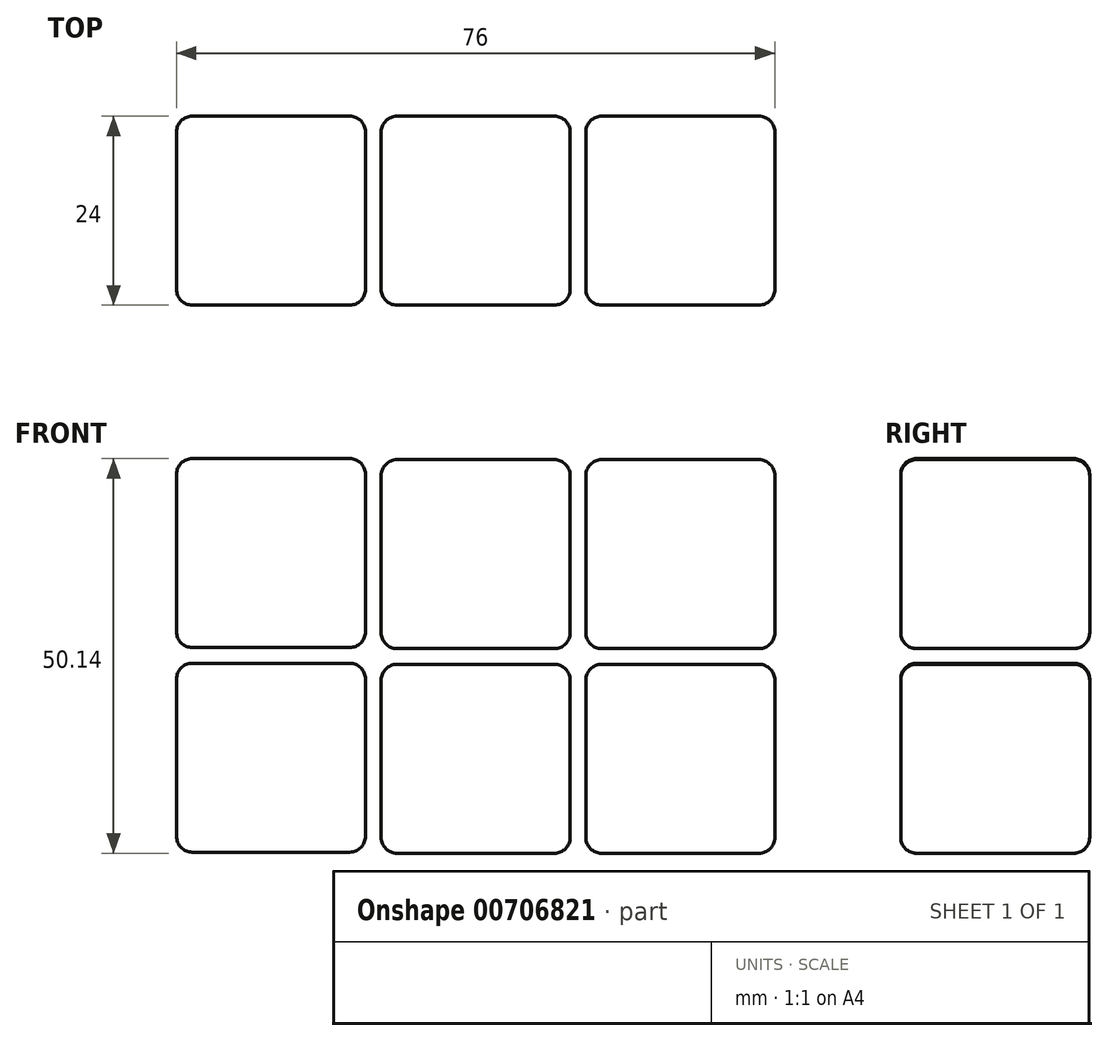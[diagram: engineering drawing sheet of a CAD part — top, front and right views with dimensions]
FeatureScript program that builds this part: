
annotation { "Feature Type Name" : "Feature", "Feature Type Description" : "" }
export const myFeature = defineFeature(function(context is Context, id is Id, definition is map)
    precondition{}
    {
        {
            var Q0;
            Q0=qCreatedBy(makeId("Front.planeOp"),FACE);
            var sketch = newSketch(context, id + "F0", { "sketchPlane" : qUnion([Q0])});
            skLineSegment(sketch, "E0.bottom", {"start": v(-63.14, 48.94) * mm, "end": v(-43.14, 48.94) * mm});
            skLineSegment(sketch, "E0.top", {"start": v(-63.14, 24.94) * mm, "end": v(-43.14, 24.94) * mm});
            skLineSegment(sketch, "E0.left", {"start": v(-65.14, 46.94) * mm, "end": v(-65.14, 26.94) * mm});
            skLineSegment(sketch, "E0.right", {"start": v(-41.14, 46.94) * mm, "end": v(-41.14, 26.94) * mm});
            skPoint(sketch, "E1.visualSharp", {"position": v(-65.14, 48.94) * mm});
            skArc(sketch, "E1.filletArc", {"start": v(-63.14, 48.94) * mm, "mid": v(-64.55, 48.36) * mm, "end": v(-65.14, 46.94) * mm});
            skPoint(sketch, "E2.visualSharp", {"position": v(-41.14, 48.94) * mm});
            skArc(sketch, "E2.filletArc", {"start": v(-41.14, 46.94) * mm, "mid": v(-41.72, 48.36) * mm, "end": v(-43.14, 48.94) * mm});
            skPoint(sketch, "E3.visualSharp", {"position": v(-41.14, 24.94) * mm});
            skArc(sketch, "E3.filletArc", {"start": v(-43.14, 24.94) * mm, "mid": v(-41.72, 25.53) * mm, "end": v(-41.14, 26.94) * mm});
            skPoint(sketch, "E4.visualSharp", {"position": v(-65.14, 24.94) * mm});
            skArc(sketch, "E4.filletArc", {"start": v(-65.14, 26.94) * mm, "mid": v(-64.55, 25.53) * mm, "end": v(-63.14, 24.94) * mm});
            skLineSegment(sketch, "E5.bottom", {"start": v(-63.14, 22.94) * mm, "end": v(-43.14, 22.94) * mm});
            skLineSegment(sketch, "E5.top", {"start": v(-63.14, -1.06) * mm, "end": v(-43.14, -1.06) * mm});
            skLineSegment(sketch, "E5.left", {"start": v(-65.14, 20.94) * mm, "end": v(-65.14, 0.94) * mm});
            skLineSegment(sketch, "E5.right", {"start": v(-41.14, 20.94) * mm, "end": v(-41.14, 0.94) * mm});
            skPoint(sketch, "E6.visualSharp", {"position": v(-65.14, 22.94) * mm});
            skArc(sketch, "E6.filletArc", {"start": v(-63.14, 22.94) * mm, "mid": v(-64.55, 22.36) * mm, "end": v(-65.14, 20.94) * mm});
            skPoint(sketch, "E7.visualSharp", {"position": v(-41.14, 22.94) * mm});
            skArc(sketch, "E7.filletArc", {"start": v(-41.14, 20.94) * mm, "mid": v(-41.72, 22.36) * mm, "end": v(-43.14, 22.94) * mm});
            skPoint(sketch, "E8.visualSharp", {"position": v(-41.14, -1.06) * mm});
            skArc(sketch, "E8.filletArc", {"start": v(-43.14, -1.06) * mm, "mid": v(-41.72, -0.47) * mm, "end": v(-41.14, 0.94) * mm});
            skPoint(sketch, "E9.visualSharp", {"position": v(-65.14, -1.06) * mm});
            skArc(sketch, "E9.filletArc", {"start": v(-65.14, 0.94) * mm, "mid": v(-64.55, -0.47) * mm, "end": v(-63.14, -1.06) * mm});
            skLineSegment(sketch, "E10.bottom", {"start": v(-89.14, 48.94) * mm, "end": v(-69.14, 48.94) * mm});
            skLineSegment(sketch, "E10.top", {"start": v(-89.14, 24.94) * mm, "end": v(-69.14, 24.94) * mm});
            skLineSegment(sketch, "E10.left", {"start": v(-91.14, 46.94) * mm, "end": v(-91.14, 26.94) * mm});
            skLineSegment(sketch, "E10.right", {"start": v(-67.14, 46.94) * mm, "end": v(-67.14, 26.94) * mm});
            skPoint(sketch, "E11.visualSharp", {"position": v(-91.14, 48.94) * mm});
            skArc(sketch, "E11.filletArc", {"start": v(-89.14, 48.94) * mm, "mid": v(-90.55, 48.36) * mm, "end": v(-91.14, 46.94) * mm});
            skPoint(sketch, "E12.visualSharp", {"position": v(-67.14, 48.94) * mm});
            skArc(sketch, "E12.filletArc", {"start": v(-67.14, 46.94) * mm, "mid": v(-67.72, 48.36) * mm, "end": v(-69.14, 48.94) * mm});
            skPoint(sketch, "E13.visualSharp", {"position": v(-67.14, 24.94) * mm});
            skArc(sketch, "E13.filletArc", {"start": v(-69.14, 24.94) * mm, "mid": v(-67.72, 25.53) * mm, "end": v(-67.14, 26.94) * mm});
            skPoint(sketch, "E14.visualSharp", {"position": v(-91.14, 24.94) * mm});
            skArc(sketch, "E14.filletArc", {"start": v(-91.14, 26.94) * mm, "mid": v(-90.55, 25.53) * mm, "end": v(-89.14, 24.94) * mm});
            skLineSegment(sketch, "E15.bottom", {"start": v(-89.14, 22.94) * mm, "end": v(-69.14, 22.94) * mm});
            skLineSegment(sketch, "E15.top", {"start": v(-89.14, -1.06) * mm, "end": v(-69.14, -1.06) * mm});
            skLineSegment(sketch, "E15.left", {"start": v(-91.14, 20.94) * mm, "end": v(-91.14, 0.94) * mm});
            skLineSegment(sketch, "E15.right", {"start": v(-67.14, 20.94) * mm, "end": v(-67.14, 0.94) * mm});
            skPoint(sketch, "E16.visualSharp", {"position": v(-91.14, 22.94) * mm});
            skArc(sketch, "E16.filletArc", {"start": v(-89.14, 22.94) * mm, "mid": v(-90.55, 22.36) * mm, "end": v(-91.14, 20.94) * mm});
            skPoint(sketch, "E17.visualSharp", {"position": v(-67.14, 22.94) * mm});
            skArc(sketch, "E17.filletArc", {"start": v(-67.14, 20.94) * mm, "mid": v(-67.72, 22.36) * mm, "end": v(-69.14, 22.94) * mm});
            skPoint(sketch, "E18.visualSharp", {"position": v(-67.14, -1.06) * mm});
            skArc(sketch, "E18.filletArc", {"start": v(-69.14, -1.06) * mm, "mid": v(-67.72, -0.47) * mm, "end": v(-67.14, 0.94) * mm});
            skPoint(sketch, "E19.visualSharp", {"position": v(-91.14, -1.06) * mm});
            skArc(sketch, "E19.filletArc", {"start": v(-91.14, 0.94) * mm, "mid": v(-90.55, -0.47) * mm, "end": v(-89.14, -1.06) * mm});
            skLineSegment(sketch, "E20.bottom", {"start": v(-115.14, 49.08) * mm, "end": v(-95.14, 49.08) * mm});
            skLineSegment(sketch, "E20.top", {"start": v(-115.14, 25.08) * mm, "end": v(-95.14, 25.08) * mm});
            skLineSegment(sketch, "E20.left", {"start": v(-117.14, 47.08) * mm, "end": v(-117.14, 27.08) * mm});
            skLineSegment(sketch, "E20.right", {"start": v(-93.14, 47.08) * mm, "end": v(-93.14, 27.08) * mm});
            skPoint(sketch, "E21.visualSharp", {"position": v(-117.14, 49.08) * mm});
            skArc(sketch, "E21.filletArc", {"start": v(-115.14, 49.08) * mm, "mid": v(-116.55, 48.5) * mm, "end": v(-117.14, 47.08) * mm});
            skPoint(sketch, "E22.visualSharp", {"position": v(-93.14, 49.08) * mm});
            skArc(sketch, "E22.filletArc", {"start": v(-93.14, 47.08) * mm, "mid": v(-93.72, 48.5) * mm, "end": v(-95.14, 49.08) * mm});
            skPoint(sketch, "E23.visualSharp", {"position": v(-93.14, 25.08) * mm});
            skArc(sketch, "E23.filletArc", {"start": v(-95.14, 25.08) * mm, "mid": v(-93.72, 25.67) * mm, "end": v(-93.14, 27.08) * mm});
            skPoint(sketch, "E24.visualSharp", {"position": v(-117.14, 25.08) * mm});
            skArc(sketch, "E24.filletArc", {"start": v(-117.14, 27.08) * mm, "mid": v(-116.55, 25.67) * mm, "end": v(-115.14, 25.08) * mm});
            skLineSegment(sketch, "E25.bottom", {"start": v(-115.14, 23.08) * mm, "end": v(-95.14, 23.08) * mm});
            skLineSegment(sketch, "E25.top", {"start": v(-115.14, -0.92) * mm, "end": v(-95.14, -0.92) * mm});
            skLineSegment(sketch, "E25.left", {"start": v(-117.14, 21.08) * mm, "end": v(-117.14, 1.08) * mm});
            skLineSegment(sketch, "E25.right", {"start": v(-93.14, 21.08) * mm, "end": v(-93.14, 1.08) * mm});
            skPoint(sketch, "E26.visualSharp", {"position": v(-117.14, 23.08) * mm});
            skArc(sketch, "E26.filletArc", {"start": v(-115.14, 23.08) * mm, "mid": v(-116.55, 22.5) * mm, "end": v(-117.14, 21.08) * mm});
            skPoint(sketch, "E27.visualSharp", {"position": v(-93.14, 23.08) * mm});
            skArc(sketch, "E27.filletArc", {"start": v(-93.14, 21.08) * mm, "mid": v(-93.72, 22.5) * mm, "end": v(-95.14, 23.08) * mm});
            skPoint(sketch, "E28.visualSharp", {"position": v(-93.14, -0.92) * mm});
            skArc(sketch, "E28.filletArc", {"start": v(-95.14, -0.92) * mm, "mid": v(-93.72, -0.33) * mm, "end": v(-93.14, 1.08) * mm});
            skPoint(sketch, "E29.visualSharp", {"position": v(-117.14, -0.92) * mm});
            skArc(sketch, "E29.filletArc", {"start": v(-117.14, 1.08) * mm, "mid": v(-116.55, -0.33) * mm, "end": v(-115.14, -0.92) * mm});
            skSolve(sketch);
        }
        {
            var Q0;
            Q0 = qSketchRegion(id + "F0", true);
            extrude(context, id + "F1", {"entities" : qUnion([Q0]), "depth" : 24 * mm, "offsetDistance" : 25 * mm});
        }
        {
            var Q0;
            Q0=makeQuery(id+"F1.opExtrude","CAP_FACE",FACE,{"disambiguationData":[OSD([sQuery(id+"F0.wireOp",EDGE,"E25.bottom"),sQuery(id+"F0.wireOp",EDGE,"E25.top"),sQuery(id+"F0.wireOp",EDGE,"E25.left"),sQuery(id+"F0.wireOp",EDGE,"E25.right"),sQuery(id+"F0.wireOp",EDGE,"E26.filletArc"),sQuery(id+"F0.wireOp",EDGE,"E27.filletArc"),sQuery(id+"F0.wireOp",EDGE,"E28.filletArc"),sQuery(id+"F0.wireOp",EDGE,"E29.filletArc")])],"isStart":false});
            var Q1;
            Q1=makeQuery(id+"F1.opExtrude","CAP_FACE",FACE,{"disambiguationData":[OSD([sQuery(id+"F0.wireOp",EDGE,"E15.bottom"),sQuery(id+"F0.wireOp",EDGE,"E15.top"),sQuery(id+"F0.wireOp",EDGE,"E15.left"),sQuery(id+"F0.wireOp",EDGE,"E15.right"),sQuery(id+"F0.wireOp",EDGE,"E16.filletArc"),sQuery(id+"F0.wireOp",EDGE,"E17.filletArc"),sQuery(id+"F0.wireOp",EDGE,"E18.filletArc"),sQuery(id+"F0.wireOp",EDGE,"E19.filletArc")])],"isStart":false});
            var Q2;
            Q2=makeQuery(id+"F1.opExtrude","CAP_FACE",FACE,{"disambiguationData":[OSD([sQuery(id+"F0.wireOp",EDGE,"E5.bottom"),sQuery(id+"F0.wireOp",EDGE,"E5.top"),sQuery(id+"F0.wireOp",EDGE,"E5.left"),sQuery(id+"F0.wireOp",EDGE,"E5.right"),sQuery(id+"F0.wireOp",EDGE,"E6.filletArc"),sQuery(id+"F0.wireOp",EDGE,"E7.filletArc"),sQuery(id+"F0.wireOp",EDGE,"E8.filletArc"),sQuery(id+"F0.wireOp",EDGE,"E9.filletArc")])],"isStart":false});
            var Q3;
            Q3=makeQuery(id+"F1.opExtrude","CAP_FACE",FACE,{"disambiguationData":[OSD([sQuery(id+"F0.wireOp",EDGE,"E0.bottom"),sQuery(id+"F0.wireOp",EDGE,"E0.top"),sQuery(id+"F0.wireOp",EDGE,"E0.left"),sQuery(id+"F0.wireOp",EDGE,"E0.right"),sQuery(id+"F0.wireOp",EDGE,"E1.filletArc"),sQuery(id+"F0.wireOp",EDGE,"E2.filletArc"),sQuery(id+"F0.wireOp",EDGE,"E3.filletArc"),sQuery(id+"F0.wireOp",EDGE,"E4.filletArc")])],"isStart":false});
            var Q4;
            Q4=makeQuery(id+"F1.opExtrude","CAP_FACE",FACE,{"disambiguationData":[OSD([sQuery(id+"F0.wireOp",EDGE,"E10.bottom"),sQuery(id+"F0.wireOp",EDGE,"E10.top"),sQuery(id+"F0.wireOp",EDGE,"E10.left"),sQuery(id+"F0.wireOp",EDGE,"E10.right"),sQuery(id+"F0.wireOp",EDGE,"E11.filletArc"),sQuery(id+"F0.wireOp",EDGE,"E12.filletArc"),sQuery(id+"F0.wireOp",EDGE,"E13.filletArc"),sQuery(id+"F0.wireOp",EDGE,"E14.filletArc")])],"isStart":false});
            var Q5;
            Q5=makeQuery(id+"F1.opExtrude","CAP_FACE",FACE,{"disambiguationData":[OSD([sQuery(id+"F0.wireOp",EDGE,"E20.bottom"),sQuery(id+"F0.wireOp",EDGE,"E20.top"),sQuery(id+"F0.wireOp",EDGE,"E20.left"),sQuery(id+"F0.wireOp",EDGE,"E20.right"),sQuery(id+"F0.wireOp",EDGE,"E21.filletArc"),sQuery(id+"F0.wireOp",EDGE,"E22.filletArc"),sQuery(id+"F0.wireOp",EDGE,"E23.filletArc"),sQuery(id+"F0.wireOp",EDGE,"E24.filletArc")])],"isStart":false});
            var Q6;
            Q6=makeQuery(id+"F1.opExtrude","CAP_FACE",FACE,{"disambiguationData":[OSD([sQuery(id+"F0.wireOp",EDGE,"E15.bottom"),sQuery(id+"F0.wireOp",EDGE,"E15.top"),sQuery(id+"F0.wireOp",EDGE,"E15.left"),sQuery(id+"F0.wireOp",EDGE,"E15.right"),sQuery(id+"F0.wireOp",EDGE,"E16.filletArc"),sQuery(id+"F0.wireOp",EDGE,"E17.filletArc"),sQuery(id+"F0.wireOp",EDGE,"E18.filletArc"),sQuery(id+"F0.wireOp",EDGE,"E19.filletArc")])],"isStart":true});
            var Q7;
            Q7=makeQuery(id+"F1.opExtrude","CAP_FACE",FACE,{"disambiguationData":[OSD([sQuery(id+"F0.wireOp",EDGE,"E5.bottom"),sQuery(id+"F0.wireOp",EDGE,"E5.top"),sQuery(id+"F0.wireOp",EDGE,"E5.left"),sQuery(id+"F0.wireOp",EDGE,"E5.right"),sQuery(id+"F0.wireOp",EDGE,"E6.filletArc"),sQuery(id+"F0.wireOp",EDGE,"E7.filletArc"),sQuery(id+"F0.wireOp",EDGE,"E8.filletArc"),sQuery(id+"F0.wireOp",EDGE,"E9.filletArc")])],"isStart":true});
            var Q8;
            Q8=makeQuery(id+"F1.opExtrude","CAP_FACE",FACE,{"disambiguationData":[OSD([sQuery(id+"F0.wireOp",EDGE,"E0.bottom"),sQuery(id+"F0.wireOp",EDGE,"E0.top"),sQuery(id+"F0.wireOp",EDGE,"E0.left"),sQuery(id+"F0.wireOp",EDGE,"E0.right"),sQuery(id+"F0.wireOp",EDGE,"E1.filletArc"),sQuery(id+"F0.wireOp",EDGE,"E2.filletArc"),sQuery(id+"F0.wireOp",EDGE,"E3.filletArc"),sQuery(id+"F0.wireOp",EDGE,"E4.filletArc")])],"isStart":true});
            var Q9;
            Q9=makeQuery(id+"F1.opExtrude","CAP_FACE",FACE,{"disambiguationData":[OSD([sQuery(id+"F0.wireOp",EDGE,"E10.bottom"),sQuery(id+"F0.wireOp",EDGE,"E10.top"),sQuery(id+"F0.wireOp",EDGE,"E10.left"),sQuery(id+"F0.wireOp",EDGE,"E10.right"),sQuery(id+"F0.wireOp",EDGE,"E11.filletArc"),sQuery(id+"F0.wireOp",EDGE,"E12.filletArc"),sQuery(id+"F0.wireOp",EDGE,"E13.filletArc"),sQuery(id+"F0.wireOp",EDGE,"E14.filletArc")])],"isStart":true});
            var Q10;
            Q10=makeQuery(id+"F1.opExtrude","CAP_FACE",FACE,{"disambiguationData":[OSD([sQuery(id+"F0.wireOp",EDGE,"E20.bottom"),sQuery(id+"F0.wireOp",EDGE,"E20.top"),sQuery(id+"F0.wireOp",EDGE,"E20.left"),sQuery(id+"F0.wireOp",EDGE,"E20.right"),sQuery(id+"F0.wireOp",EDGE,"E21.filletArc"),sQuery(id+"F0.wireOp",EDGE,"E22.filletArc"),sQuery(id+"F0.wireOp",EDGE,"E23.filletArc"),sQuery(id+"F0.wireOp",EDGE,"E24.filletArc")])],"isStart":true});
            var Q11;
            Q11=makeQuery(id+"F1.opExtrude","CAP_FACE",FACE,{"disambiguationData":[OSD([sQuery(id+"F0.wireOp",EDGE,"E25.bottom"),sQuery(id+"F0.wireOp",EDGE,"E25.top"),sQuery(id+"F0.wireOp",EDGE,"E25.left"),sQuery(id+"F0.wireOp",EDGE,"E25.right"),sQuery(id+"F0.wireOp",EDGE,"E26.filletArc"),sQuery(id+"F0.wireOp",EDGE,"E27.filletArc"),sQuery(id+"F0.wireOp",EDGE,"E28.filletArc"),sQuery(id+"F0.wireOp",EDGE,"E29.filletArc")])],"isStart":true});
            fillet(context, id + "F2", {"entities" : qUnion([Q0, Q1, Q2, Q3, Q4, Q5, Q6, Q7, Q8, Q9, Q10, Q11]), "radius" : 2 * mm, "tangentPropagation" : true, "allowEdgeOverflow" : false});
        }
    });
